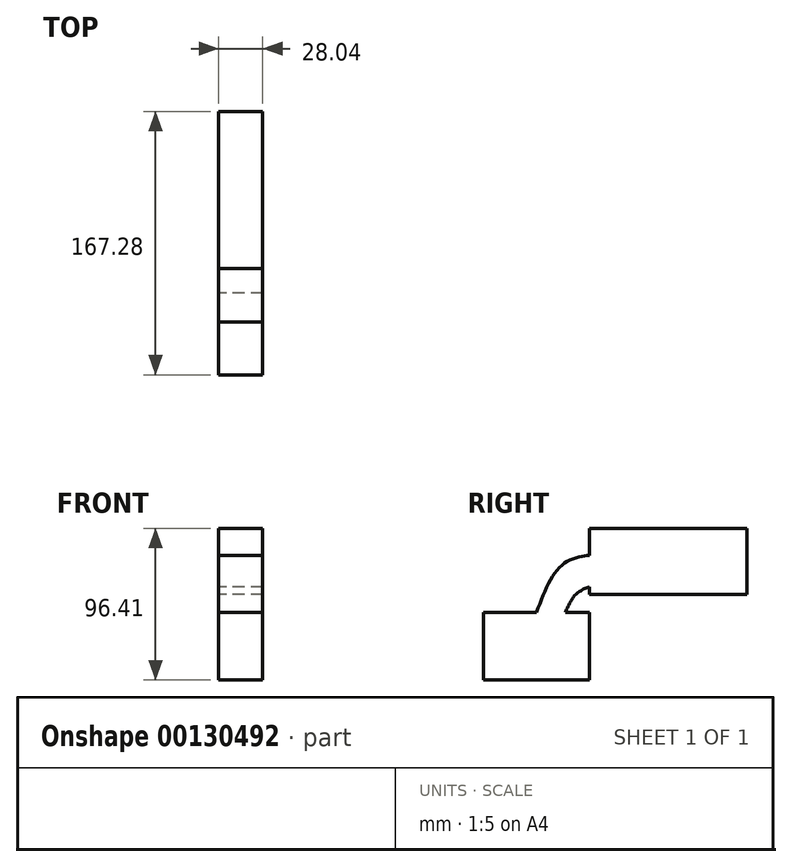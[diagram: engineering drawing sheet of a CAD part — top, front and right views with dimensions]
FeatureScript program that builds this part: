
annotation { "Feature Type Name" : "Feature", "Feature Type Description" : "" }
export const myFeature = defineFeature(function(context is Context, id is Id, definition is map)
    precondition{}
    {
        {
            var Q0;
            Q0=qCreatedBy(makeId("Right.planeOp"),FACE);
            var sketch = newSketch(context, id + "F0", { "sketchPlane" : qUnion([Q0])});
            skLineSegment(sketch, "E0.bottom", {"start": v(-67.38, -5.66) * mm, "end": v(0, -5.66) * mm});
            skLineSegment(sketch, "E0.top", {"start": v(-67.38, -48.64) * mm, "end": v(0, -48.64) * mm});
            skLineSegment(sketch, "E0.left", {"start": v(-67.38, -5.66) * mm, "end": v(-67.38, -48.64) * mm});
            skLineSegment(sketch, "E0.right", {"start": v(0, -5.66) * mm, "end": v(0, -48.64) * mm});
            skFitSpline(sketch, "E1", {"points": [v(-33.69, -5.66) * mm, v(-17.13, 24.83) * mm, v(0, 30.64) * mm, v(4.07, 31.22) * mm, v(2.9, 31.51) * mm], "startDerivative": vector(30.68, 82.94) * mm, "endDerivative": vector(-20.67, 3.59) * mm});
            skFitSpline(sketch, "E2", {"points": [v(-15.4, -5.66) * mm, v(-7.84, 6.61) * mm, v(4.94, 12.05) * mm, v(12.2, 13.8) * mm], "startDerivative": vector(15.76, 37.45) * mm, "endDerivative": vector(24.61, 5.65) * mm});
            skLineSegment(sketch, "E3.bottom", {"start": v(0, 47.77) * mm, "end": v(99.9, 47.77) * mm});
            skLineSegment(sketch, "E3.top", {"start": v(0, 5.66) * mm, "end": v(99.9, 5.66) * mm});
            skLineSegment(sketch, "E3.left", {"start": v(0, 47.77) * mm, "end": v(0, 5.66) * mm});
            skLineSegment(sketch, "E3.right", {"start": v(99.9, 47.77) * mm, "end": v(99.9, 5.66) * mm});
            skSolve(sketch);
        }
        {
            var Q0;
            {var subQ3=sQuery(id+"F0.wireOp",EDGE,"E3.bottom");Q0=makeQuery(id+"F0.imprint","IMPRINT",FACE,{"disambiguationData":[TD([[makeQuery(id+"F0.imprint","IMPRINT",EDGE,{"derivedFrom":subQ3}),-1.0]])]});}
            var Q1;
            {var subQ0=sQuery(id+"F0.wireOp",EDGE,"E1");var subQ1=sQuery(id+"F0.wireOp",EDGE,"E0.bottom");var subQ2=makeQuery(id+"F0.imprint","INTERSECT",VERTEX,{"derivedFrom":[subQ1,subQ0]});Q1=makeQuery(id+"F0.imprint","IMPRINT",FACE,{"disambiguationData":[TD([[makeQuery(id+"F0.imprint","IMPRINT",EDGE,{"disambiguationData":[TD([[subQ2,-1.0]])],"derivedFrom":subQ1}),1.0]])]});}
            var Q2;
            Q2=makeQuery(id+"F0.imprint","IMPRINT",FACE,{"disambiguationData":[TD([[makeQuery(id+"F0.imprint","IMPRINT",EDGE,{"derivedFrom":sQuery(id+"F0.wireOp",EDGE,"E0.top")}),1.0]])]});
            extrude(context, id + "F1", {"entities" : qUnion([Q0, Q1, Q2]), "endBound" : BoundingType.SYMMETRIC, "depth" : 28.05 * mm});
        }
    });
